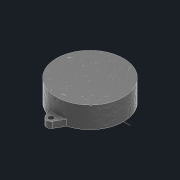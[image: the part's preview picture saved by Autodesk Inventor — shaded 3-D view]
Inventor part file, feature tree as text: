
AUTODESK INVENTOR PART (.ipt)
format: ipt  version: 2022 (Build 260153000, 153)  size: 116,736 bytes
history: native  units: mm
features: extrude x3, sketch x2, hole x1
ambient origin geometry x8: Origin, YZ Plane, XZ Plane, XY Plane, X Axis, Y Axis, Z Axis, Center Point
bodies: Solid1 (feature_tree)
feature tree (6):
  sketch  "Sketch1"  dims[d0=44.0mm d1=60.0deg]
  extrude  "Extrusion1"  TaperAngle=60.0deg  [1 undecoded]
  extrude  "Extrusion2"  Depth=3.0mm
  hole  "Hole1"  [1 undecoded]
  extrude  "Extrusion3"  Depth=4.0mm TaperAngle=0.0deg
  sketch  "Sketch2"  dims[d2=6.0mm d3=51.0mm d4=14.0mm d5=0.0mm d6=4.0mm d7=0.0mm d8=3.4mm d9=6.0mm d10=6.5mm d11=3.4mm d12=90.0deg d13=8.0mm d14=20.594885mm d15=8.0mm d16=3.0mm d17=0.0mm]
note: 2 required parameter values undecoded (feature->parameter linkage not recoverable at this tier; creation-order binding heuristic only, values carry confidence <= 0.55)
